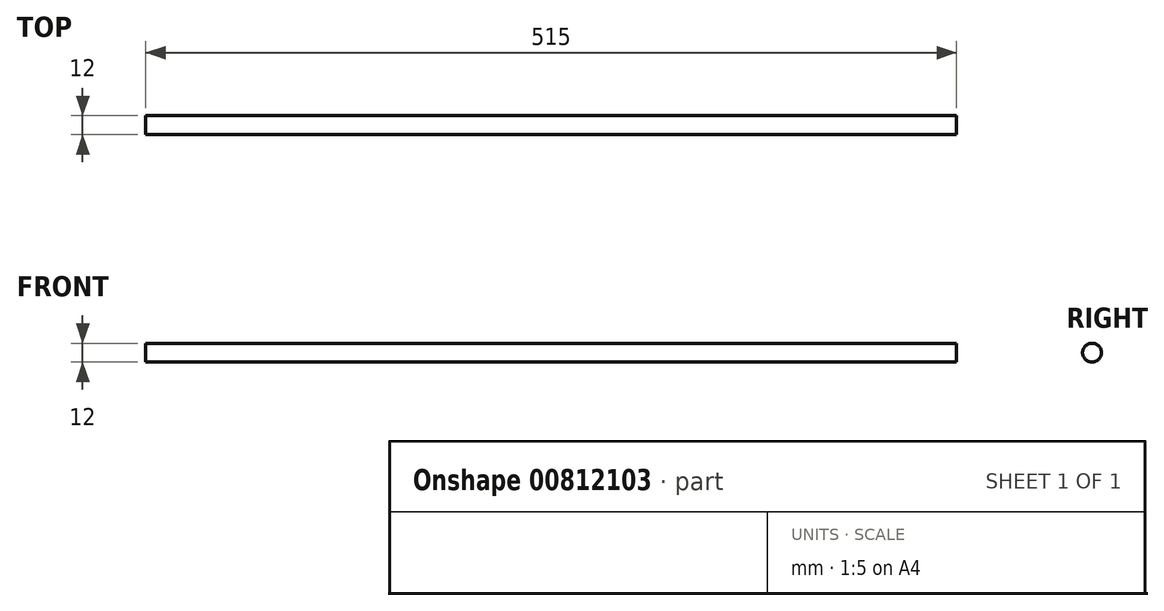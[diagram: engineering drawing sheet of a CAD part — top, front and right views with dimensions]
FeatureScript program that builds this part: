
annotation { "Feature Type Name" : "Feature", "Feature Type Description" : "" }
export const myFeature = defineFeature(function(context is Context, id is Id, definition is map)
    precondition{}
    {
        {
            var Q0;
            Q0=qCreatedBy(makeId("Right.planeOp"),FACE);
            var sketch = newSketch(context, id + "F0", { "sketchPlane" : qUnion([Q0])});
            skCircle(sketch, "E0", {"center": v(0, 0) * mm, "radius": 6 * mm});
            skSolve(sketch);
        }
        {
            var Q0;
            Q0=qSketchRegion(id+"F0",true);
            extrude(context, id + "F1", {"entities" : qUnion([Q0]), "depth" : 515 * mm, "symmetric" : true});
        }
    });
